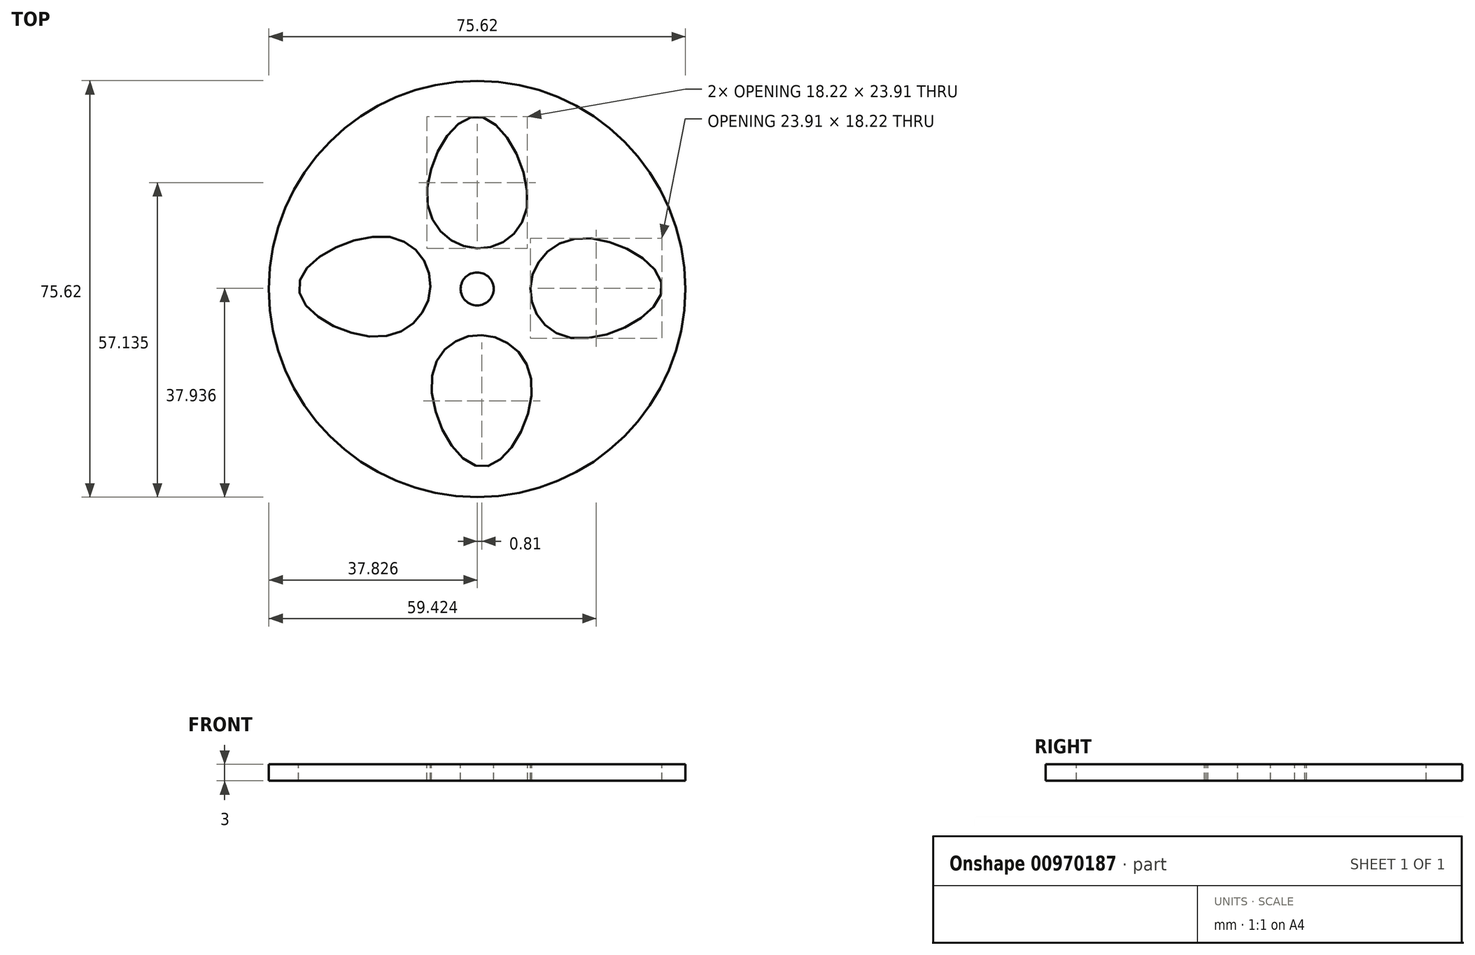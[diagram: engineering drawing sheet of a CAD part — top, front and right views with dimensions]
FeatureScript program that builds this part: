
annotation { "Feature Type Name" : "Feature", "Feature Type Description" : "" }
export const myFeature = defineFeature(function(context is Context, id is Id, definition is map)
    precondition{}
    {
        {
            var Q0;
            Q0=qCreatedBy(makeId("Top.planeOp"),FACE);
            var sketch = newSketch(context, id + "F0", { "sketchPlane" : qUnion([Q0])});
            skCircle(sketch, "E0", {"center": v(0, 0) * mm, "radius": 37.8 * mm});
            skSolve(sketch);
        }
        {
            var Q0;
            Q0=makeQuery(id+"F0.imprint","IMPRINT",FACE,{"disambiguationData":[TD([[makeQuery(id+"F0.imprint","IMPRINT",EDGE,{"derivedFrom":sQuery(id+"F0.wireOp",EDGE,"E0")}),1.0]])]});
            extrude(context, id + "F1", {"entities" : qUnion([Q0]), "depth" : 3 * mm, "offsetDistance" : 25 * mm});
        }
        {
            var Q0;
            Q0=makeQuery(id+"F1.opExtrude","CAP_FACE",FACE,{"disambiguationData":[OSD([sQuery(id+"F0.wireOp",EDGE,"E0")])],"isStart":false});
            var sketch = newSketch(context, id + "F2", { "sketchPlane" : qUnion([Q0])});
            skCircle(sketch, "E1", {"center": v(0, 0) * mm, "radius": 3.2 * mm});
            skSolve(sketch);
        }
        {
            var Q0;
            Q0=sQuery(id+"F2.wireOp",VERTEX,"E1.center");
            var Q1;
            Q1=makeQuery(id+"F1.opExtrude","SWEPT_BODY",BODY,{"disambiguationData":[OSD([sQuery(id+"F0.wireOp",EDGE,"E0")])]});
            hole(context, id + "F3", {"style" : HoleStyle.SIMPLE, "endStyle" : HoleEndStyle.THROUGH, "holeDiameter" : 6 * mm, "majorDiameter" : 5 * mm, "isTappedThrough" : true, "tappedDepth" : 12 * mm, "tapClearance" : 3, "locations" : qUnion([Q0]), "scope" : qUnion([Q1])});
        }
        {
            var Q0;
            Q0=makeQuery(id+"F1.opExtrude","CAP_FACE",FACE,{"disambiguationData":[OSD([sQuery(id+"F0.wireOp",EDGE,"E0")])],"isStart":false});
            var sketch = newSketch(context, id + "F4", { "sketchPlane" : qUnion([Q0])});
            skFitSpline(sketch, "E2", {"points": [v(0, 7.37) * mm, v(-9.06, 16.06) * mm, v(0, 31.28) * mm, v(9.06, 15.1) * mm, v(0, 7.37) * mm]});
            skFitSpline(sketch, "E3", {"points": [v(0.84, -8.36) * mm, v(9.9, -17.05) * mm, v(0.84, -32.27) * mm, v(-8.22, -16.09) * mm, v(0.84, -8.36) * mm]});
            skFitSpline(sketch, "E4", {"points": [v(-8.48, 0.42) * mm, v(-17.18, -8.64) * mm, v(-32.4, 0.42) * mm, v(-16.21, 9.48) * mm, v(-8.48, 0.42) * mm]});
            skFitSpline(sketch, "E5", {"points": [v(9.66, 0.14) * mm, v(18.35, 9.2) * mm, v(33.57, 0.14) * mm, v(17.39, -8.92) * mm, v(9.66, 0.14) * mm]});
            skSolve(sketch);
        }
        {
            var Q0;
            Q0=makeQuery(id+"F4.imprint","IMPRINT",FACE,{"disambiguationData":[TD([[makeQuery(id+"F4.imprint","IMPRINT",EDGE,{"derivedFrom":sQuery(id+"F4.wireOp",EDGE,"E2")}),-1.0]])]});
            var Q1;
            Q1=makeQuery(id+"F4.imprint","IMPRINT",FACE,{"disambiguationData":[TD([[makeQuery(id+"F4.imprint","IMPRINT",EDGE,{"derivedFrom":sQuery(id+"F4.wireOp",EDGE,"E4")}),-1.0]])]});
            var Q2;
            Q2=makeQuery(id+"F4.imprint","IMPRINT",FACE,{"disambiguationData":[TD([[makeQuery(id+"F4.imprint","IMPRINT",EDGE,{"derivedFrom":sQuery(id+"F4.wireOp",EDGE,"E3")}),-1.0]])]});
            var Q3;
            Q3=makeQuery(id+"F4.imprint","IMPRINT",FACE,{"disambiguationData":[TD([[makeQuery(id+"F4.imprint","IMPRINT",EDGE,{"derivedFrom":sQuery(id+"F4.wireOp",EDGE,"E5")}),-1.0]])]});
            extrude(context, id + "F5", {"entities" : qUnion([Q0, Q1, Q2, Q3]), "operationType" : NewBodyOperationType.REMOVE, "oppositeDirection" : true, "depth" : 3 * mm, "offsetDistance" : 25 * mm});
        }
    });
